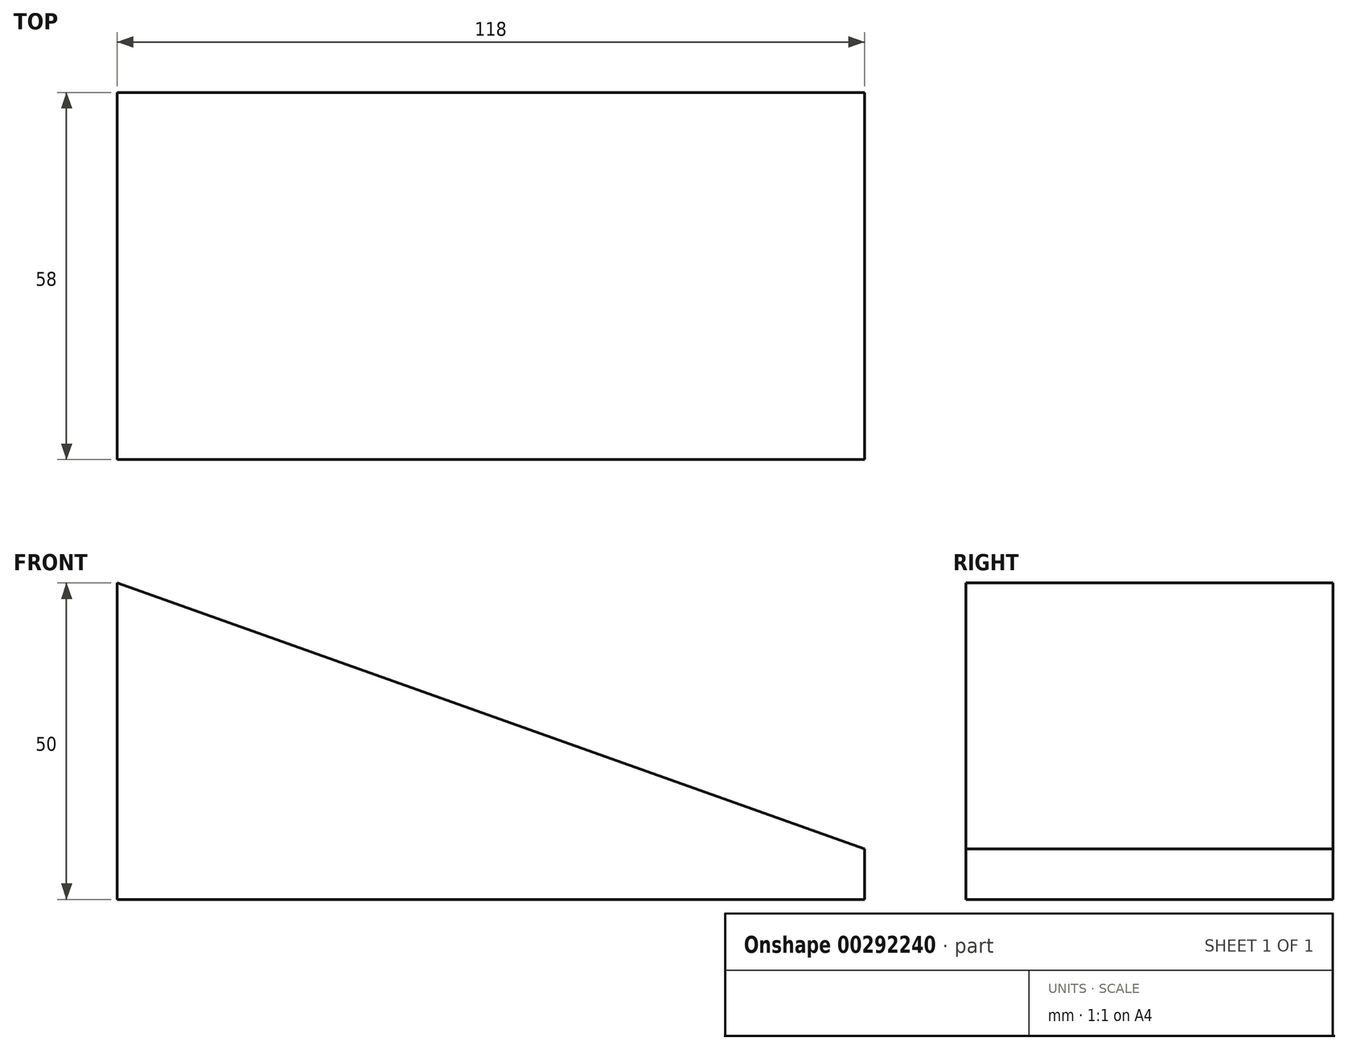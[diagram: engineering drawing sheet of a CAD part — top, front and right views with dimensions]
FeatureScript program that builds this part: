
annotation { "Feature Type Name" : "Feature", "Feature Type Description" : "" }
export const myFeature = defineFeature(function(context is Context, id is Id, definition is map)
    precondition{}
    {
        {
            var Q0;
            Q0=qCreatedBy(makeId("Front.planeOp"),FACE);
            var sketch = newSketch(context, id + "F0", { "sketchPlane" : qUnion([Q0])});
            skLineSegment(sketch, "E0", {"start": v(0, 0) * mm, "end": v(118, 0) * mm});
            skLineSegment(sketch, "E1", {"start": v(118, 0) * mm, "end": v(118, 8) * mm});
            skLineSegment(sketch, "E2", {"start": v(0, 0) * mm, "end": v(0, 50) * mm});
            skLineSegment(sketch, "E3", {"start": v(0, 50) * mm, "end": v(118, 8) * mm});
            skSolve(sketch);
        }
        {
            var Q0;
            Q0=makeQuery(id+"F0.imprint","IMPRINT",FACE,{"disambiguationData":[TD([[makeQuery(id+"F0.imprint","IMPRINT",EDGE,{"derivedFrom":sQuery(id+"F0.wireOp",EDGE,"E0")}),1.0]])]});
            extrude(context, id + "F1", {"entities" : qUnion([Q0]), "depth" : 58 * mm});
        }
        {
            var Q0;
            Q0=qCreatedBy(makeId("Top.planeOp"),FACE);
            cPlane(context, id + "F2", {"entities" : qUnion([Q0]), "cplaneType" : CPlaneType.OFFSET, "offset" : 56 * mm, "width" : 150 * mm, "height" : 150 * mm});
        }
    });
